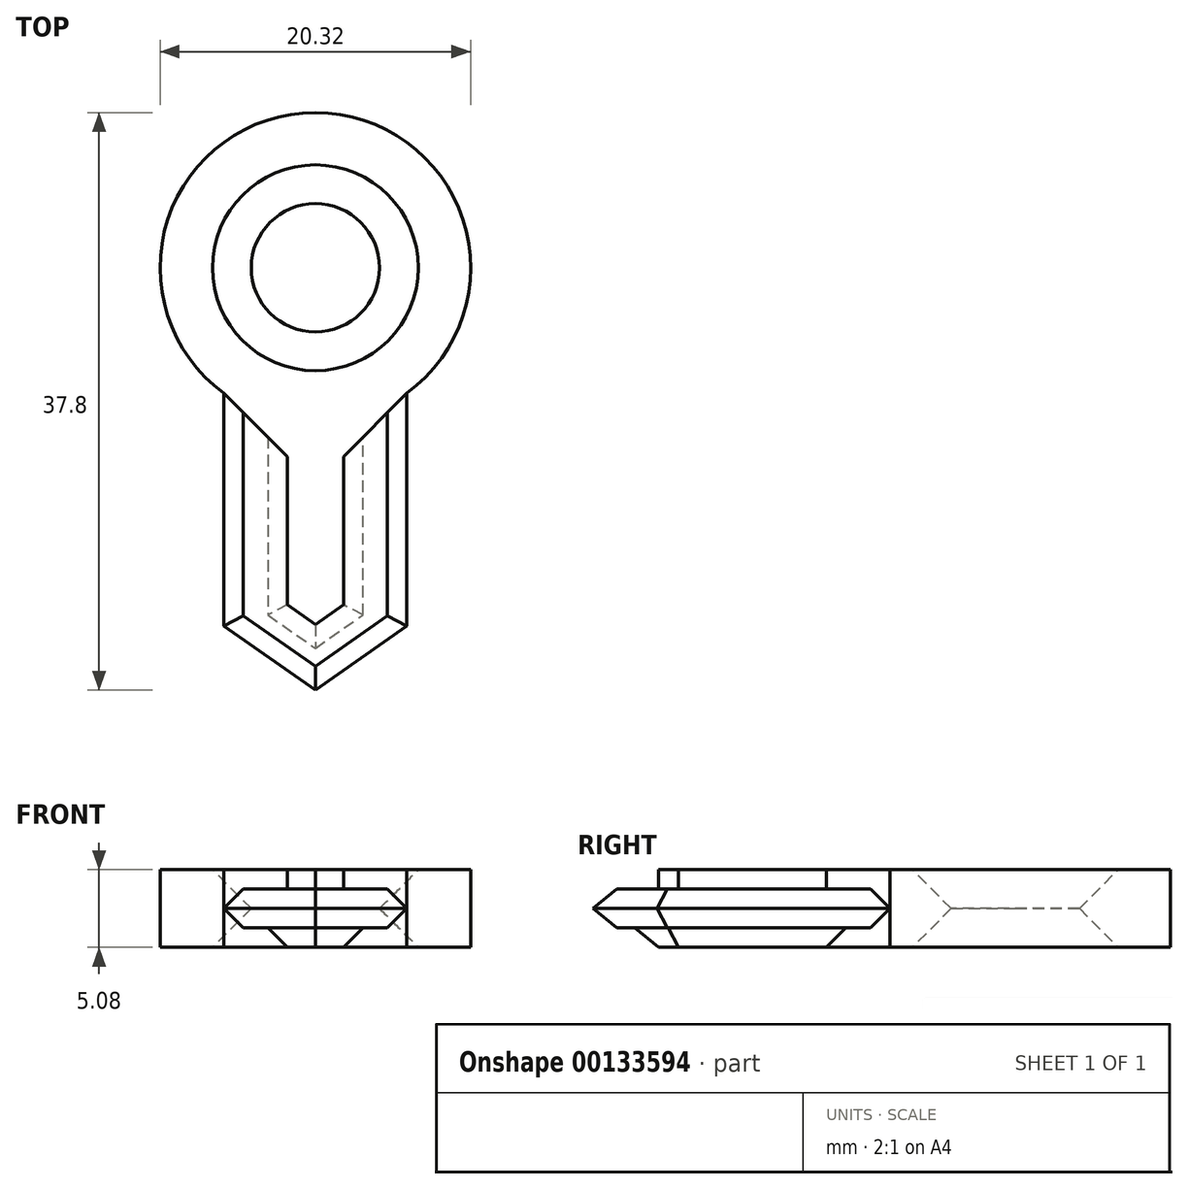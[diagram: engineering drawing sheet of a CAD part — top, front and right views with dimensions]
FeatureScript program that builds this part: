
annotation { "Feature Type Name" : "Feature", "Feature Type Description" : "" }
export const myFeature = defineFeature(function(context is Context, id is Id, definition is map)
    precondition{}
    {
        {
            var Q0;
            Q0=qCreatedBy(makeId("Top.planeOp"),FACE);
            var sketch = newSketch(context, id + "F0", { "sketchPlane" : qUnion([Q0])});
            skLineSegment(sketch, "E0", {"start": v(-5.98, 31.35) * mm, "end": v(-5.98, 16.11) * mm});
            skLineSegment(sketch, "E1", {"start": v(-5.98, 16.11) * mm, "end": v(0, 11.92) * mm});
            skArc(sketch, "E2", {"start": v(0, 49.72) * mm, "mid": v(-9.66, 42.7) * mm, "end": v(-5.98, 31.35) * mm});
            skLineSegment(sketch, "E3.MirrorCS", {"start": v(5.98, 31.35) * mm, "end": v(5.98, 16.11) * mm});
            skLineSegment(sketch, "E4.MirrorCS", {"start": v(5.98, 16.11) * mm, "end": v(0, 11.92) * mm});
            skArc(sketch, "E5.MirrorCS", {"start": v(0, 49.72) * mm, "mid": v(9.66, 42.7) * mm, "end": v(5.98, 31.35) * mm});
            skCircle(sketch, "E6", {"center": v(0, 39.56) * mm, "radius": 4.2 * mm});
            skLineSegment(sketch, "E7", {"start": v(1.84, 27.2) * mm, "end": v(1.84, 17.5) * mm});
            skLineSegment(sketch, "E8", {"start": v(1.84, 17.5) * mm, "end": v(0, 16.22) * mm});
            skLineSegment(sketch, "E9.MirrorCS", {"start": v(-1.84, 17.5) * mm, "end": v(0, 16.22) * mm});
            skLineSegment(sketch, "E10.MirrorCS", {"start": v(-1.84, 27.2) * mm, "end": v(-1.84, 17.5) * mm});
            skLineSegment(sketch, "E11", {"start": v(5.98, 31.35) * mm, "end": v(1.84, 27.2) * mm});
            skLineSegment(sketch, "E12", {"start": v(-5.98, 31.35) * mm, "end": v(-1.84, 27.2) * mm});
            skSolve(sketch);
        }
        {
            var Q0;
            Q0=makeQuery(id+"F0.imprint","IMPRINT",FACE,{"disambiguationData":[TD([[makeQuery(id+"F0.imprint","IMPRINT",EDGE,{"derivedFrom":sQuery(id+"F0.wireOp",EDGE,"E2")}),1.0]])]});
            extrude(context, id + "F1", {"entities" : qUnion([Q0]), "endBound" : BoundingType.SYMMETRIC, "depth" : 5.08 * mm});
        }
        {
            var Q0;
            Q0=makeQuery(id+"F0.imprint","IMPRINT",FACE,{"disambiguationData":[TD([[makeQuery(id+"F0.imprint","IMPRINT",EDGE,{"derivedFrom":sQuery(id+"F0.wireOp",EDGE,"E0")}),1.0]])]});
            extrude(context, id + "F2", {"entities" : qUnion([Q0]), "operationType" : NewBodyOperationType.ADD, "endBound" : BoundingType.SYMMETRIC, "depth" : 2.54 * mm});
        }
        {
            var Q0;
            Q0=makeQuery(id+"F2.opExtrude","CAP_EDGE",EDGE,{"disambiguationData":[OSD([sQuery(id+"F0.wireOp",EDGE,"E8")])],"isStart":false});
            var Q1;
            Q1=makeQuery(id+"F2.opExtrude","CAP_EDGE",EDGE,{"disambiguationData":[OSD([sQuery(id+"F0.wireOp",EDGE,"E9.MirrorCS")])],"isStart":false});
            var Q2;
            Q2=makeQuery(id+"F2.opExtrude","CAP_EDGE",EDGE,{"disambiguationData":[OSD([sQuery(id+"F0.wireOp",EDGE,"E7")])],"isStart":false});
            var Q3;
            Q3=makeQuery(id+"F2.opExtrude","CAP_EDGE",EDGE,{"disambiguationData":[OSD([sQuery(id+"F0.wireOp",EDGE,"E10.MirrorCS")])],"isStart":false});
            var Q4;
            Q4=makeQuery(id+"F2.opExtrude","CAP_EDGE",EDGE,{"disambiguationData":[OSD([sQuery(id+"F0.wireOp",EDGE,"E3.MirrorCS")])],"isStart":false});
            var Q5;
            Q5=makeQuery(id+"F2.opExtrude","CAP_EDGE",EDGE,{"disambiguationData":[OSD([sQuery(id+"F0.wireOp",EDGE,"E0")])],"isStart":false});
            var Q6;
            Q6=makeQuery(id+"F2.opExtrude","CAP_EDGE",EDGE,{"disambiguationData":[OSD([sQuery(id+"F0.wireOp",EDGE,"E1")])],"isStart":false});
            var Q7;
            Q7=makeQuery(id+"F2.opExtrude","CAP_EDGE",EDGE,{"disambiguationData":[OSD([sQuery(id+"F0.wireOp",EDGE,"E4.MirrorCS")])],"isStart":false});
            var Q8;
            Q8=makeQuery(id+"F2.opExtrude","CAP_EDGE",EDGE,{"disambiguationData":[OSD([sQuery(id+"F0.wireOp",EDGE,"E4.MirrorCS")])],"isStart":true});
            var Q9;
            Q9=makeQuery(id+"F2.opExtrude","CAP_EDGE",EDGE,{"disambiguationData":[OSD([sQuery(id+"F0.wireOp",EDGE,"E3.MirrorCS")])],"isStart":true});
            var Q10;
            Q10=makeQuery(id+"F2.opExtrude","CAP_EDGE",EDGE,{"disambiguationData":[OSD([sQuery(id+"F0.wireOp",EDGE,"E8")])],"isStart":true});
            var Q11;
            Q11=makeQuery(id+"F2.opExtrude","CAP_EDGE",EDGE,{"disambiguationData":[OSD([sQuery(id+"F0.wireOp",EDGE,"E7")])],"isStart":true});
            var Q12;
            Q12=makeQuery(id+"F2.opExtrude","CAP_EDGE",EDGE,{"disambiguationData":[OSD([sQuery(id+"F0.wireOp",EDGE,"E9.MirrorCS")])],"isStart":true});
            var Q13;
            Q13=makeQuery(id+"F2.opExtrude","CAP_EDGE",EDGE,{"disambiguationData":[OSD([sQuery(id+"F0.wireOp",EDGE,"E10.MirrorCS")])],"isStart":true});
            var Q14;
            Q14=makeQuery(id+"F2.opExtrude","CAP_EDGE",EDGE,{"disambiguationData":[OSD([sQuery(id+"F0.wireOp",EDGE,"E0")])],"isStart":true});
            var Q15;
            Q15=makeQuery(id+"F2.opExtrude","CAP_EDGE",EDGE,{"disambiguationData":[OSD([sQuery(id+"F0.wireOp",EDGE,"E1")])],"isStart":true});
            chamfer(context, id + "F3", {"entities" : qUnion([Q0, Q1, Q2, Q3, Q4, Q5, Q6, Q7, Q8, Q9, Q10, Q11, Q12, Q13, Q14, Q15]), "width" : 1.27 * mm, "tangentPropagation" : true});
        }
        {
            var Q0;
            Q0=makeQuery(id+"F1.opExtrude","CAP_EDGE",EDGE,{"disambiguationData":[OSD([sQuery(id+"F0.wireOp",EDGE,"E6")])],"isStart":false});
            var Q1;
            Q1=makeQuery(id+"F1.opExtrude","CAP_EDGE",EDGE,{"disambiguationData":[OSD([sQuery(id+"F0.wireOp",EDGE,"E6")])],"isStart":true});
            chamfer(context, id + "F4", {"entities" : qUnion([Q0, Q1]), "width" : 2.54 * mm, "tangentPropagation" : true});
        }
    });
